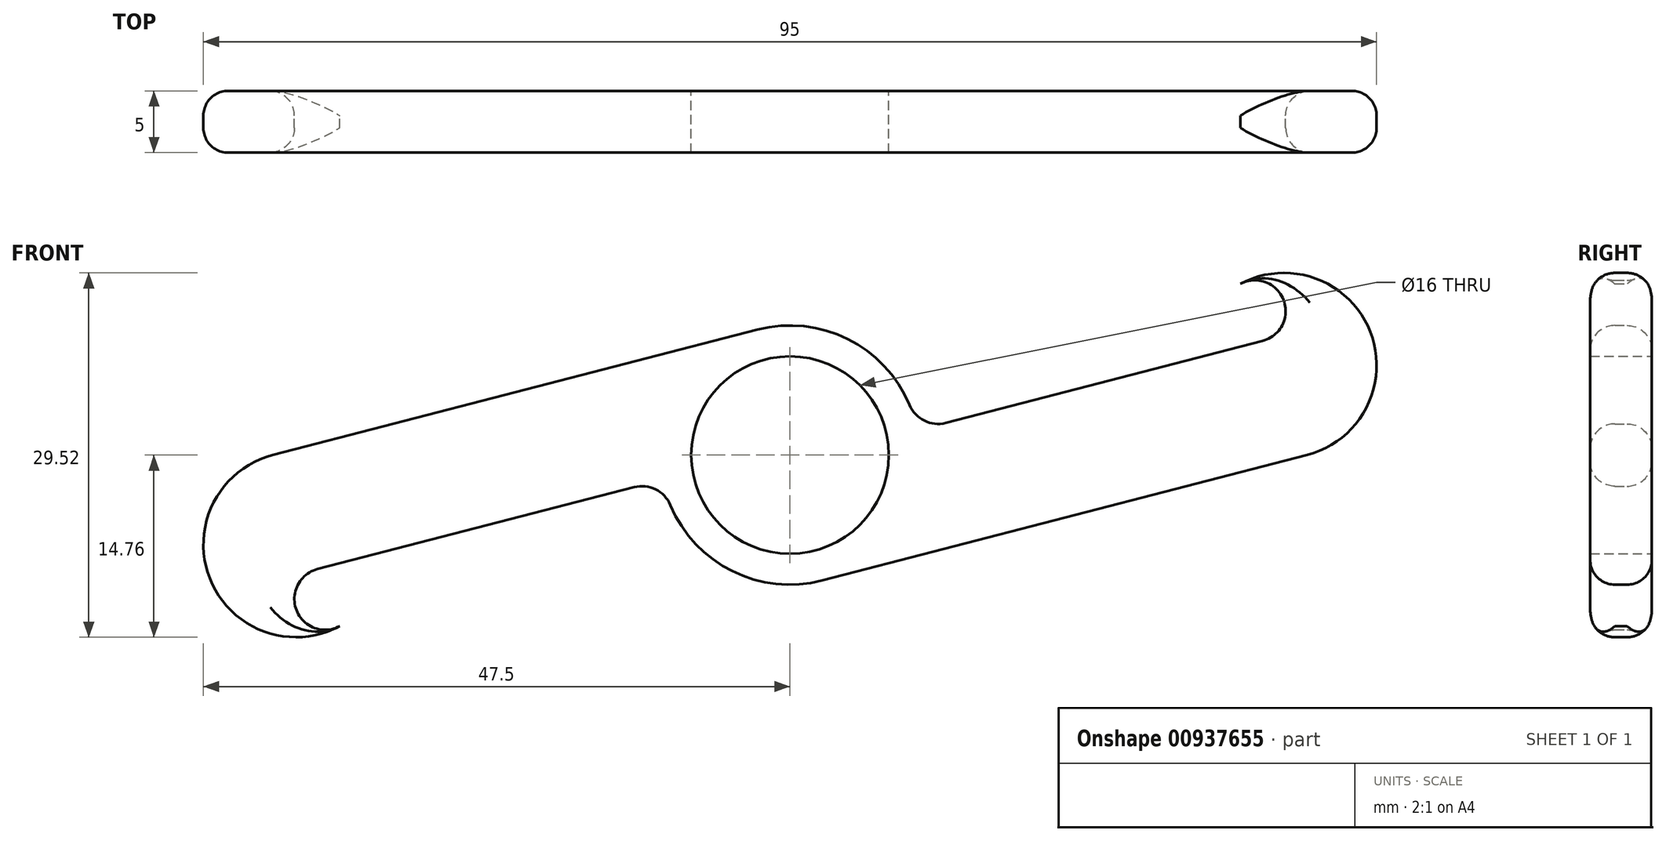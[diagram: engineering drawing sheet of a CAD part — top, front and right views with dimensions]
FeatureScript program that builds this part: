
annotation { "Feature Type Name" : "Feature", "Feature Type Description" : "" }
export const myFeature = defineFeature(function(context is Context, id is Id, definition is map)
    precondition{}
    {
        {
            var Q0;
            Q0=qCreatedBy(makeId("Front.planeOp"),FACE);
            var sketch = newSketch(context, id + "F0", { "sketchPlane" : qUnion([Q0])});
            skArc(sketch, "E0", {"start": v(-32.52, -7.76) * mm, "mid": v(-32.5, -7.5) * mm, "end": v(-32.5, -7.26) * mm});
            skLineSegment(sketch, "E1", {"start": v(-41.88, 0) * mm, "end": v(-2.63, 10.16) * mm});
            skLineSegment(sketch, "E2", {"start": v(0, 15.02) * mm, "end": v(0, -16.36) * mm, "construction": true});
            skLineSegment(sketch, "E3", {"start": v(-13.84, 0) * mm, "end": v(17.38, 0) * mm, "construction": true});
            skLineSegment(sketch, "E4", {"start": v(-40, 6.59) * mm, "end": v(-40, -22.62) * mm, "construction": true});
            skLineSegment(sketch, "E5", {"start": v(-26.01, -7.26) * mm, "end": v(-53.97, -7.26) * mm, "construction": true});
            skLineSegment(sketch, "E6", {"start": v(-32.52, -7.76) * mm, "end": v(-12.62, -2.6) * mm});
            skLineSegment(sketch, "E7", {"start": v(-32.52, -7.76) * mm, "end": v(-38.26, -9.25) * mm});
            skArc(sketch, "E8", {"start": v(-38.26, -9.25) * mm, "mid": v(-39.96, -12.58) * mm, "end": v(-36.45, -13.87) * mm});
            skArc(sketch, "E9", {"start": v(-9.68, -4.06) * mm, "mid": v(-10.88, -2.78) * mm, "end": v(-12.62, -2.6) * mm});
            skArc(sketch, "E10.trimOffspring", {"start": v(-41.88, 0) * mm, "mid": v(-46.98, -10) * mm, "end": v(-36.45, -13.87) * mm});
            skLineSegment(sketch, "E11.MirrorCS", {"start": v(41.88, 0) * mm, "end": v(2.63, -10.16) * mm});
            skLineSegment(sketch, "E12.MirrorCS", {"start": v(32.52, 7.76) * mm, "end": v(12.62, 2.6) * mm});
            skArc(sketch, "E13.MirrorCS", {"start": v(9.68, 4.06) * mm, "mid": v(10.88, 2.78) * mm, "end": v(12.62, 2.6) * mm});
            skArc(sketch, "E14.MirrorCS", {"start": v(41.88, 0) * mm, "mid": v(46.98, 10) * mm, "end": v(36.45, 13.87) * mm});
            skArc(sketch, "E15.MirrorCS", {"start": v(38.26, 9.25) * mm, "mid": v(39.96, 12.58) * mm, "end": v(36.45, 13.87) * mm});
            skLineSegment(sketch, "E16.MirrorCS", {"start": v(32.52, 7.76) * mm, "end": v(38.26, 9.25) * mm});
            skPoint(sketch, "E17.MirrorCS.start.orphan", {"position": v(41.88, 0) * mm});
            skLineSegment(sketch, "E18.MirrorCS", {"start": v(40, -6.59) * mm, "end": v(40, 22.62) * mm, "construction": true});
            skLineSegment(sketch, "E19.MirrorCS", {"start": v(26.01, 7.26) * mm, "end": v(53.97, 7.26) * mm, "construction": true});
            skArc(sketch, "E20", {"start": v(-9.68, -4.06) * mm, "mid": v(-4.66, -9.4) * mm, "end": v(2.63, -10.16) * mm});
            skArc(sketch, "E21.trimOffspring", {"start": v(9.68, 4.06) * mm, "mid": v(4.66, 9.4) * mm, "end": v(-2.63, 10.16) * mm});
            skCircle(sketch, "E22", {"center": v(0, 0) * mm, "radius": 8 * mm});
            skSolve(sketch);
        }
        {
            var Q0;
            Q0 = qSketchRegion(id + "F0", true);
            extrude(context, id + "F1", {"entities" : qUnion([Q0]), "depth" : 5 * mm, "offsetDistance" : 25 * mm});
        }
        {
            var Q0;
            Q0=makeQuery(id+"F1.opExtrude","CAP_EDGE",EDGE,{"disambiguationData":[OSD([sQuery(id+"F0.wireOp",EDGE,"E12.MirrorCS"),sQuery(id+"F0.wireOp",EDGE,"E16.MirrorCS")])],"isStart":true});
            var Q1;
            Q1=makeQuery(id+"F1.opExtrude","CAP_EDGE",EDGE,{"disambiguationData":[OSD([sQuery(id+"F0.wireOp",EDGE,"E14.MirrorCS")])],"isStart":true});
            var Q2;
            Q2=makeQuery(id+"F1.opExtrude","CAP_EDGE",EDGE,{"disambiguationData":[OSD([sQuery(id+"F0.wireOp",EDGE,"E1")])],"isStart":false});
            var Q3;
            Q3=makeQuery(id+"F1.opExtrude","CAP_EDGE",EDGE,{"disambiguationData":[OSD([sQuery(id+"F0.wireOp",EDGE,"E11.MirrorCS")])],"isStart":false});
            fillet(context, id + "F2", {"entities" : qUnion([Q0, Q1, Q2, Q3]), "radius" : 2 * mm, "tangentPropagation" : true, "allowEdgeOverflow" : false});
        }
    });
